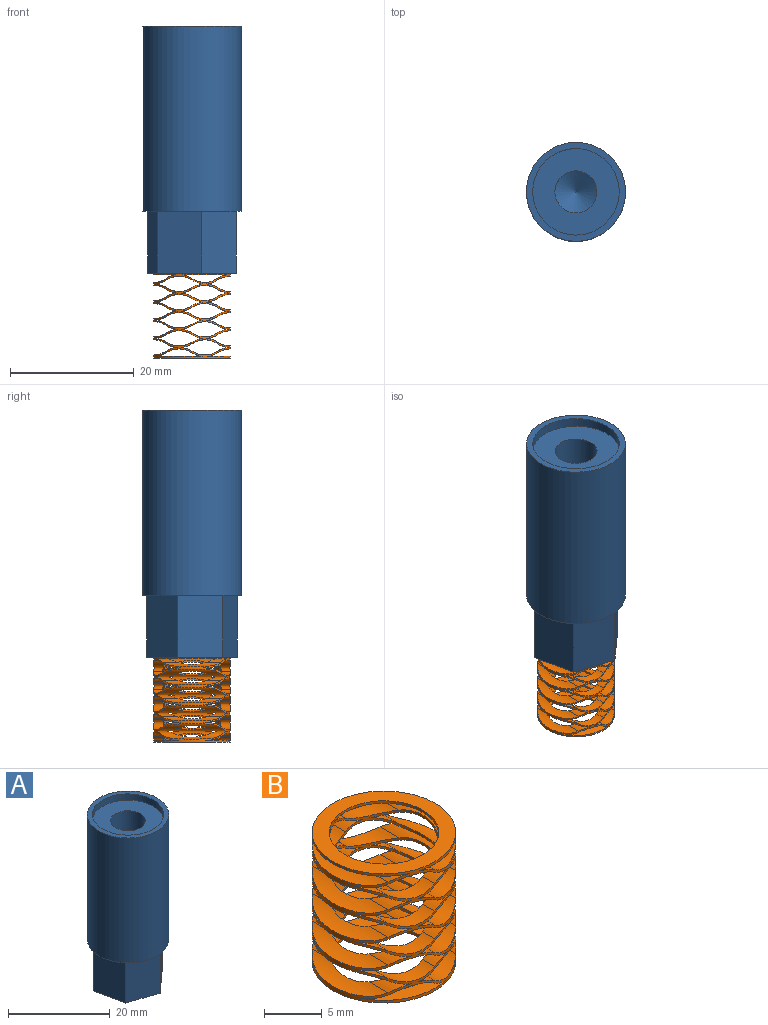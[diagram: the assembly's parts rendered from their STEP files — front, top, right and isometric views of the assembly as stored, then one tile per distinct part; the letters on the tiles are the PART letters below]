
ASSEMBLY  parts=2 mates=1
PART A: 14 faces, bbox 16x16x40 mm
  f0: cylinder r=8mm len=30mm, axis (0,0,-1), area 1508mm2, adj f1,f12
  f1: plane 16x16mm, normal (0,0,1), area 47.1mm2, adj f0,f2
  f2: cylinder r=7mm len=14mm, axis (0,0,1), area 66mm2, adj f1,f3
  f3: plane 14x14mm, normal (0,0,1), area 117.6mm2, adj f2,f5
  f4: cone r=0mm half-angle=59deg, axis (0,0,1), area 42.4mm2, adj f5
  f5: cylinder r=3.4mm len=25mm, axis (0,0,1), area 534.1mm2, adj f3,f4
  f6: plane 10x7.13mm, normal (-0.31,-0.95,0), area 75.1mm2, adj f7,f11,f12,f13
  f7: plane 10x5.59mm, normal (0.67,-0.74,0), area 75.1mm2, adj f6,f8,f12,f13
  f8: plane 10x7.34mm, normal (0.98,0.21,0), area 75.1mm2, adj f7,f9,f12,f13
  f9: plane 10x7.13mm, normal (0.31,0.95,0), area 75.1mm2, adj f8,f10,f12,f13
  f10: plane 10x5.59mm, normal (-0.67,0.74,0), area 75.1mm2, adj f9,f11,f12,f13
  f11: plane 10x7.34mm, normal (-0.98,-0.21,0), area 75.1mm2, adj f6,f10,f12,f13
  f12: plane 16x16mm, normal (0,0,-1), area 54.7mm2, adj f0,f6,f7,f8,f9,f10,f11
  f13: plane 14.69x14.27mm, normal (0,0,-1), area 146.4mm2, adj f6,f7,f8,f9,f10,f11
PART B: 152 faces, bbox 12.4x12.4x13.7 mm
  f0: plane 12.45x12.45mm, normal (0,0,1), area 50.8mm2, adj f150,f151
  f1: plane 12.45x7.43mm, normal (0,0,-1), area 29mm2, adj f4,f5,f6,f150,f151
  f2: cylinder r=3.85mm len=4.15mm, axis (0,1,0), area 7.4mm2, adj f5,f6,f150,f151
  f3: cylinder r=3.85mm len=4.15mm, axis (0,1,0), area 7.4mm2, adj f4,f6,f150,f151
  f4: cylinder r=3.72mm len=1.77mm, axis (0,1,0), area 2.7mm2, adj f1,f3,f150,f151
  f5: cylinder r=3.72mm len=1.77mm, axis (0,1,0), area 2.7mm2, adj f1,f2,f150,f151
  f6: cylinder r=3.72mm len=9.28mm, axis (0,1,0), area 10.9mm2, adj f1,f2,f3,f150,f151
  f7: cylinder r=3.85mm len=9.28mm, axis (0,1,0), area 12.1mm2, adj f9,f10,f150,f151
  f8: plane 11.39x3.71mm, normal (0,0,-1), area 17.7mm2, adj f9,f10,f150,f151
  f9: cylinder r=3.72mm len=3.38mm, axis (0,1,0), area 3.3mm2, adj f7,f8,f150,f151
  f10: cylinder r=3.72mm len=3.38mm, axis (0,1,0), area 3.3mm2, adj f7,f8,f150,f151
  f11: cylinder r=3.72mm len=9.28mm, axis (0,1,0), area 12.2mm2, adj f12,f13,f150,f151
  f12: cylinder r=3.85mm len=3.43mm, axis (0,1,0), area 3.5mm2, adj f11,f15,f150,f151
  f13: cylinder r=3.85mm len=3.43mm, axis (0,1,0), area 3.5mm2, adj f11,f16,f150,f151
  f14: cylinder r=3.72mm len=9.28mm, axis (0,1,0), area 12.2mm2, adj f15,f16,f150,f151
  f15: cylinder r=3.85mm len=3.43mm, axis (0,1,0), area 3.5mm2, adj f12,f14,f150,f151
  f16: cylinder r=3.85mm len=3.43mm, axis (0,1,0), area 3.5mm2, adj f13,f14,f150,f151
  f17: cylinder r=3.72mm len=4.15mm, axis (0,1,0), area 7.4mm2, adj f19,f21,f150,f151
  f18: cylinder r=3.72mm len=4.15mm, axis (0,1,0), area 7.4mm2, adj f19,f20,f150,f151
  f19: cylinder r=3.85mm len=9.28mm, axis (0,1,0), area 11.3mm2, adj f17,f18,f24,f150,f151
  f20: cylinder r=3.85mm len=1.81mm, axis (0,1,0), area 2.7mm2, adj f18,f25,f150,f151
  f21: cylinder r=3.85mm len=1.81mm, axis (0,1,0), area 2.7mm2, adj f17,f26,f150,f151
  f22: cylinder r=3.72mm len=4.15mm, axis (0,1,0), area 7.4mm2, adj f24,f26,f150,f151
  f23: cylinder r=3.72mm len=4.15mm, axis (0,1,0), area 7.4mm2, adj f24,f25,f150,f151
  f24: cylinder r=3.85mm len=9.28mm, axis (0,1,0), area 11.3mm2, adj f19,f22,f23,f150,f151
  f25: cylinder r=3.85mm len=1.81mm, axis (0,1,0), area 2.7mm2, adj f20,f23,f150,f151
  f26: cylinder r=3.85mm len=1.81mm, axis (0,1,0), area 2.7mm2, adj f21,f22,f150,f151
  f27: cylinder r=3.85mm len=4.15mm, axis (0,1,0), area 7.4mm2, adj f30,f31,f150,f151
  f28: cylinder r=3.85mm len=4.15mm, axis (0,1,0), area 7.4mm2, adj f29,f31,f150,f151
  f29: cylinder r=3.72mm len=1.81mm, axis (0,1,0), area 2.7mm2, adj f28,f34,f150,f151
  f30: cylinder r=3.72mm len=1.81mm, axis (0,1,0), area 2.7mm2, adj f27,f35,f150,f151
  f31: cylinder r=3.72mm len=9.28mm, axis (0,1,0), area 11.4mm2, adj f27,f28,f36,f150,f151
  f32: cylinder r=3.85mm len=4.15mm, axis (0,1,0), area 7.4mm2, adj f35,f36,f150,f151
  f33: cylinder r=3.85mm len=4.15mm, axis (0,1,0), area 7.4mm2, adj f34,f36,f150,f151
  f34: cylinder r=3.72mm len=1.81mm, axis (0,1,0), area 2.7mm2, adj f29,f33,f150,f151
  f35: cylinder r=3.72mm len=1.81mm, axis (0,1,0), area 2.7mm2, adj f30,f32,f150,f151
  f36: cylinder r=3.72mm len=9.28mm, axis (0,1,0), area 11.4mm2, adj f31,f32,f33,f150,f151
  f37: cylinder r=3.85mm len=9.28mm, axis (0,1,0), area 12.1mm2, adj f41,f42,f150,f151
  f38: cylinder r=3.85mm len=9.28mm, axis (0,1,0), area 12.1mm2, adj f39,f40,f150,f151
  f39: cylinder r=3.72mm len=3.44mm, axis (0,1,0), area 3.5mm2, adj f38,f41,f150,f151
  f40: cylinder r=3.72mm len=3.44mm, axis (0,1,0), area 3.5mm2, adj f38,f42,f150,f151
  f41: cylinder r=3.72mm len=3.44mm, axis (0,1,0), area 3.5mm2, adj f37,f39,f150,f151
  f42: cylinder r=3.72mm len=3.44mm, axis (0,1,0), area 3.5mm2, adj f37,f40,f150,f151
  f43: cylinder r=3.72mm len=9.28mm, axis (0,1,0), area 12.2mm2, adj f44,f45,f150,f151
  f44: cylinder r=3.85mm len=3.43mm, axis (0,1,0), area 3.5mm2, adj f43,f47,f150,f151
  f45: cylinder r=3.85mm len=3.43mm, axis (0,1,0), area 3.5mm2, adj f43,f48,f150,f151
  f46: cylinder r=3.72mm len=9.28mm, axis (0,1,0), area 12.2mm2, adj f47,f48,f150,f151
  f47: cylinder r=3.85mm len=3.43mm, axis (0,1,0), area 3.5mm2, adj f44,f46,f150,f151
  f48: cylinder r=3.85mm len=3.43mm, axis (0,1,0), area 3.5mm2, adj f45,f46,f150,f151
  f49: cylinder r=3.72mm len=4.15mm, axis (0,1,0), area 7.4mm2, adj f51,f53,f150,f151
  f50: cylinder r=3.72mm len=4.15mm, axis (0,1,0), area 7.4mm2, adj f51,f52,f150,f151
  f51: cylinder r=3.85mm len=9.28mm, axis (0,1,0), area 11.3mm2, adj f49,f50,f56,f150,f151
  f52: cylinder r=3.85mm len=1.81mm, axis (0,1,0), area 2.7mm2, adj f50,f57,f150,f151
  f53: cylinder r=3.85mm len=1.81mm, axis (0,1,0), area 2.7mm2, adj f49,f58,f150,f151
  f54: cylinder r=3.72mm len=4.15mm, axis (0,1,0), area 7.4mm2, adj f56,f58,f150,f151
  f55: cylinder r=3.72mm len=4.15mm, axis (0,1,0), area 7.4mm2, adj f56,f57,f150,f151
  f56: cylinder r=3.85mm len=9.28mm, axis (0,1,0), area 11.3mm2, adj f51,f54,f55,f150,f151
  f57: cylinder r=3.85mm len=1.81mm, axis (0,1,0), area 2.7mm2, adj f52,f55,f150,f151
  f58: cylinder r=3.85mm len=1.81mm, axis (0,1,0), area 2.7mm2, adj f53,f54,f150,f151
  f59: cylinder r=3.85mm len=4.15mm, axis (0,1,0), area 7.4mm2, adj f62,f63,f150,f151
  f60: cylinder r=3.85mm len=4.15mm, axis (0,1,0), area 7.4mm2, adj f61,f63,f150,f151
  f61: cylinder r=3.72mm len=1.81mm, axis (0,1,0), area 2.7mm2, adj f60,f66,f150,f151
  f62: cylinder r=3.72mm len=1.81mm, axis (0,1,0), area 2.7mm2, adj f59,f67,f150,f151
  f63: cylinder r=3.72mm len=9.28mm, axis (0,1,0), area 11.4mm2, adj f59,f60,f68,f150,f151
  f64: cylinder r=3.85mm len=4.15mm, axis (0,1,0), area 7.4mm2, adj f67,f68,f150,f151
  f65: cylinder r=3.85mm len=4.15mm, axis (0,1,0), area 7.4mm2, adj f66,f68,f150,f151
  f66: cylinder r=3.72mm len=1.81mm, axis (0,1,0), area 2.7mm2, adj f61,f65,f150,f151
  f67: cylinder r=3.72mm len=1.81mm, axis (0,1,0), area 2.7mm2, adj f62,f64,f150,f151
  f68: cylinder r=3.72mm len=9.28mm, axis (0,1,0), area 11.4mm2, adj f63,f64,f65,f150,f151
  f69: cylinder r=3.85mm len=9.28mm, axis (0,1,0), area 12.1mm2, adj f73,f74,f150,f151
  f70: cylinder r=3.85mm len=9.28mm, axis (0,1,0), area 12.1mm2, adj f71,f72,f150,f151
  f71: cylinder r=3.72mm len=3.44mm, axis (0,1,0), area 3.5mm2, adj f70,f73,f150,f151
  f72: cylinder r=3.72mm len=3.44mm, axis (0,1,0), area 3.5mm2, adj f70,f74,f150,f151
  f73: cylinder r=3.72mm len=3.44mm, axis (0,1,0), area 3.5mm2, adj f69,f71,f150,f151
  f74: cylinder r=3.72mm len=3.44mm, axis (0,1,0), area 3.5mm2, adj f69,f72,f150,f151
  f75: cylinder r=3.72mm len=9.28mm, axis (0,1,0), area 12.2mm2, adj f76,f77,f150,f151
  f76: cylinder r=3.85mm len=3.43mm, axis (0,1,0), area 3.5mm2, adj f75,f79,f150,f151
  f77: cylinder r=3.85mm len=3.43mm, axis (0,1,0), area 3.5mm2, adj f75,f80,f150,f151
  f78: cylinder r=3.72mm len=9.28mm, axis (0,1,0), area 12.2mm2, adj f79,f80,f150,f151
  f79: cylinder r=3.85mm len=3.43mm, axis (0,1,0), area 3.5mm2, adj f76,f78,f150,f151
  f80: cylinder r=3.85mm len=3.43mm, axis (0,1,0), area 3.5mm2, adj f77,f78,f150,f151
  f81: cylinder r=3.72mm len=4.15mm, axis (0,1,0), area 7.4mm2, adj f83,f85,f150,f151
  f82: cylinder r=3.72mm len=4.15mm, axis (0,1,0), area 7.4mm2, adj f83,f84,f150,f151
  f83: cylinder r=3.85mm len=9.28mm, axis (0,1,0), area 11.3mm2, adj f81,f82,f88,f150,f151
  f84: cylinder r=3.85mm len=1.81mm, axis (0,1,0), area 2.7mm2, adj f82,f89,f150,f151
  f85: cylinder r=3.85mm len=1.81mm, axis (0,1,0), area 2.7mm2, adj f81,f90,f150,f151
  f86: cylinder r=3.72mm len=4.15mm, axis (0,1,0), area 7.4mm2, adj f88,f90,f150,f151
  f87: cylinder r=3.72mm len=4.15mm, axis (0,1,0), area 7.4mm2, adj f88,f89,f150,f151
  f88: cylinder r=3.85mm len=9.28mm, axis (0,1,0), area 11.3mm2, adj f83,f86,f87,f150,f151
  f89: cylinder r=3.85mm len=1.81mm, axis (0,1,0), area 2.7mm2, adj f84,f87,f150,f151
  f90: cylinder r=3.85mm len=1.81mm, axis (0,1,0), area 2.7mm2, adj f85,f86,f150,f151
  f91: cylinder r=3.85mm len=4.15mm, axis (0,1,0), area 7.4mm2, adj f94,f95,f150,f151
  f92: cylinder r=3.85mm len=4.15mm, axis (0,1,0), area 7.4mm2, adj f93,f95,f150,f151
  f93: cylinder r=3.72mm len=1.81mm, axis (0,1,0), area 2.7mm2, adj f92,f98,f150,f151
  f94: cylinder r=3.72mm len=1.81mm, axis (0,1,0), area 2.7mm2, adj f91,f99,f150,f151
  f95: cylinder r=3.72mm len=9.28mm, axis (0,1,0), area 11.4mm2, adj f91,f92,f100,f150,f151
  f96: cylinder r=3.85mm len=4.15mm, axis (0,1,0), area 7.4mm2, adj f99,f100,f150,f151
  f97: cylinder r=3.85mm len=4.15mm, axis (0,1,0), area 7.4mm2, adj f98,f100,f150,f151
  f98: cylinder r=3.72mm len=1.81mm, axis (0,1,0), area 2.7mm2, adj f93,f97,f150,f151
  f99: cylinder r=3.72mm len=1.81mm, axis (0,1,0), area 2.7mm2, adj f94,f96,f150,f151
  f100: cylinder r=3.72mm len=9.28mm, axis (0,1,0), area 11.4mm2, adj f95,f96,f97,f150,f151
  f101: cylinder r=3.85mm len=9.28mm, axis (0,1,0), area 12.1mm2, adj f105,f106,f150,f151
  f102: cylinder r=3.85mm len=9.28mm, axis (0,1,0), area 12.1mm2, adj f103,f104,f150,f151
  f103: cylinder r=3.72mm len=3.44mm, axis (0,1,0), area 3.5mm2, adj f102,f105,f150,f151
  f104: cylinder r=3.72mm len=3.44mm, axis (0,1,0), area 3.5mm2, adj f102,f106,f150,f151
  f105: cylinder r=3.72mm len=3.44mm, axis (0,1,0), area 3.5mm2, adj f101,f103,f150,f151
  f106: cylinder r=3.72mm len=3.44mm, axis (0,1,0), area 3.5mm2, adj f101,f104,f150,f151
  f107: cylinder r=3.72mm len=9.28mm, axis (0,1,0), area 12.2mm2, adj f108,f109,f150,f151
  f108: cylinder r=3.85mm len=3.43mm, axis (0,1,0), area 3.5mm2, adj f107,f111,f150,f151
  f109: cylinder r=3.85mm len=3.43mm, axis (0,1,0), area 3.5mm2, adj f107,f112,f150,f151
  f110: cylinder r=3.72mm len=9.28mm, axis (0,1,0), area 12.2mm2, adj f111,f112,f150,f151
  f111: cylinder r=3.85mm len=3.43mm, axis (0,1,0), area 3.5mm2, adj f108,f110,f150,f151
  f112: cylinder r=3.85mm len=3.43mm, axis (0,1,0), area 3.5mm2, adj f109,f110,f150,f151
  f113: cylinder r=3.72mm len=4.15mm, axis (0,1,0), area 7.4mm2, adj f115,f117,f150,f151
  f114: cylinder r=3.72mm len=4.15mm, axis (0,1,0), area 7.4mm2, adj f115,f116,f150,f151
  f115: cylinder r=3.85mm len=9.28mm, axis (0,1,0), area 11.3mm2, adj f113,f114,f120,f150,f151
  f116: cylinder r=3.85mm len=1.81mm, axis (0,1,0), area 2.7mm2, adj f114,f121,f150,f151
  f117: cylinder r=3.85mm len=1.81mm, axis (0,1,0), area 2.7mm2, adj f113,f122,f150,f151
  f118: cylinder r=3.72mm len=4.15mm, axis (0,1,0), area 7.4mm2, adj f120,f122,f150,f151
  f119: cylinder r=3.72mm len=4.15mm, axis (0,1,0), area 7.4mm2, adj f120,f121,f150,f151
  f120: cylinder r=3.85mm len=9.28mm, axis (0,1,0), area 11.3mm2, adj f115,f118,f119,f150,f151
  f121: cylinder r=3.85mm len=1.81mm, axis (0,1,0), area 2.7mm2, adj f116,f119,f150,f151
  f122: cylinder r=3.85mm len=1.81mm, axis (0,1,0), area 2.7mm2, adj f117,f118,f150,f151
  f123: cylinder r=3.85mm len=4.15mm, axis (0,1,0), area 7.4mm2, adj f126,f127,f150,f151
  f124: cylinder r=3.85mm len=4.15mm, axis (0,1,0), area 7.4mm2, adj f125,f127,f150,f151
  f125: cylinder r=3.72mm len=1.82mm, axis (0,1,0), area 2.8mm2, adj f124,f130,f150,f151
  f126: cylinder r=3.72mm len=1.82mm, axis (0,1,0), area 2.8mm2, adj f123,f131,f150,f151
  f127: cylinder r=3.72mm len=9.28mm, axis (0,1,0), area 11.4mm2, adj f123,f124,f132,f150,f151
  f128: cylinder r=3.85mm len=4.15mm, axis (0,1,0), area 7.4mm2, adj f131,f132,f150,f151
  f129: cylinder r=3.85mm len=4.15mm, axis (0,1,0), area 7.4mm2, adj f130,f132,f150,f151
  f130: cylinder r=3.6mm len=1.82mm, axis (0,1,0), area 2.8mm2, adj f125,f129,f150,f151
  f131: cylinder r=3.6mm len=1.82mm, axis (0,1,0), area 2.8mm2, adj f126,f128,f150,f151
  f132: cylinder r=3.6mm len=9.28mm, axis (0,1,0), area 11.5mm2, adj f127,f128,f129,f150,f151
  f133: cylinder r=3.85mm len=9.28mm, axis (0,1,0), area 12.1mm2, adj f137,f138,f150,f151
  f134: cylinder r=3.85mm len=9.28mm, axis (0,1,0), area 12.1mm2, adj f135,f136,f150,f151
  f135: cylinder r=3.72mm len=3.44mm, axis (0,1,0), area 3.5mm2, adj f134,f137,f150,f151
  f136: cylinder r=3.72mm len=3.44mm, axis (0,1,0), area 3.5mm2, adj f134,f138,f150,f151
  f137: cylinder r=3.6mm len=3.44mm, axis (0,1,0), area 3.5mm2, adj f133,f135,f150,f151
  f138: cylinder r=3.6mm len=3.44mm, axis (0,1,0), area 3.5mm2, adj f133,f136,f150,f151
  f139: cylinder r=3.6mm len=9.28mm, axis (0,1,0), area 12.3mm2, adj f140,f141,f150,f151
  f140: cylinder r=3.85mm len=3.3mm, axis (0,1,0), area 3mm2, adj f139,f142,f150,f151
  f141: cylinder r=3.85mm len=3.3mm, axis (0,1,0), area 3mm2, adj f139,f142,f150,f151
  f142: plane 11.22x3.53mm, normal (0,0,1), area 17.1mm2, adj f140,f141,f150,f151
  f143: cylinder r=3.85mm len=1.7mm, axis (0,1,0), area 2.3mm2, adj f146,f148,f150,f151
  f144: cylinder r=3.85mm len=1.7mm, axis (0,1,0), area 2.3mm2, adj f145,f148,f150,f151
  f145: cylinder r=3.6mm len=4.15mm, axis (0,1,0), area 7.5mm2, adj f144,f147,f150,f151
  f146: cylinder r=3.6mm len=4.15mm, axis (0,1,0), area 7.5mm2, adj f143,f147,f150,f151
  f147: cylinder r=3.85mm len=9.28mm, axis (0,1,0), area 9.8mm2, adj f145,f146,f148,f150,f151
  f148: plane 12.45x7.05mm, normal (0,0,1), area 27.4mm2, adj f143,f144,f147,f150,f151
  f149: plane 12.45x12.45mm, normal (0,0,-1), area 50.8mm2, adj f150,f151
  f150: cylinder r=6.22mm len=13.72mm, axis (0,0,-1), area 108.6mm2, adj f0,f1,f2,f3,f4,f5,f6,f7
  f151: cylinder r=4.75mm len=13.72mm, axis (0,0,-1), area 78.9mm2, adj f0,f1,f2,f3,f4,f5,f6,f7
PLACE A t=(-9.62,4.66,-4.2)mm
PLACE B rot(axis=(0,1,0),180deg) t=(-9.62,4.66,-4.2)mm
MATE fastened B.f150 <-> A.f0  axis (0,0,1) through (-9.62,4.66,-4.2)mm
